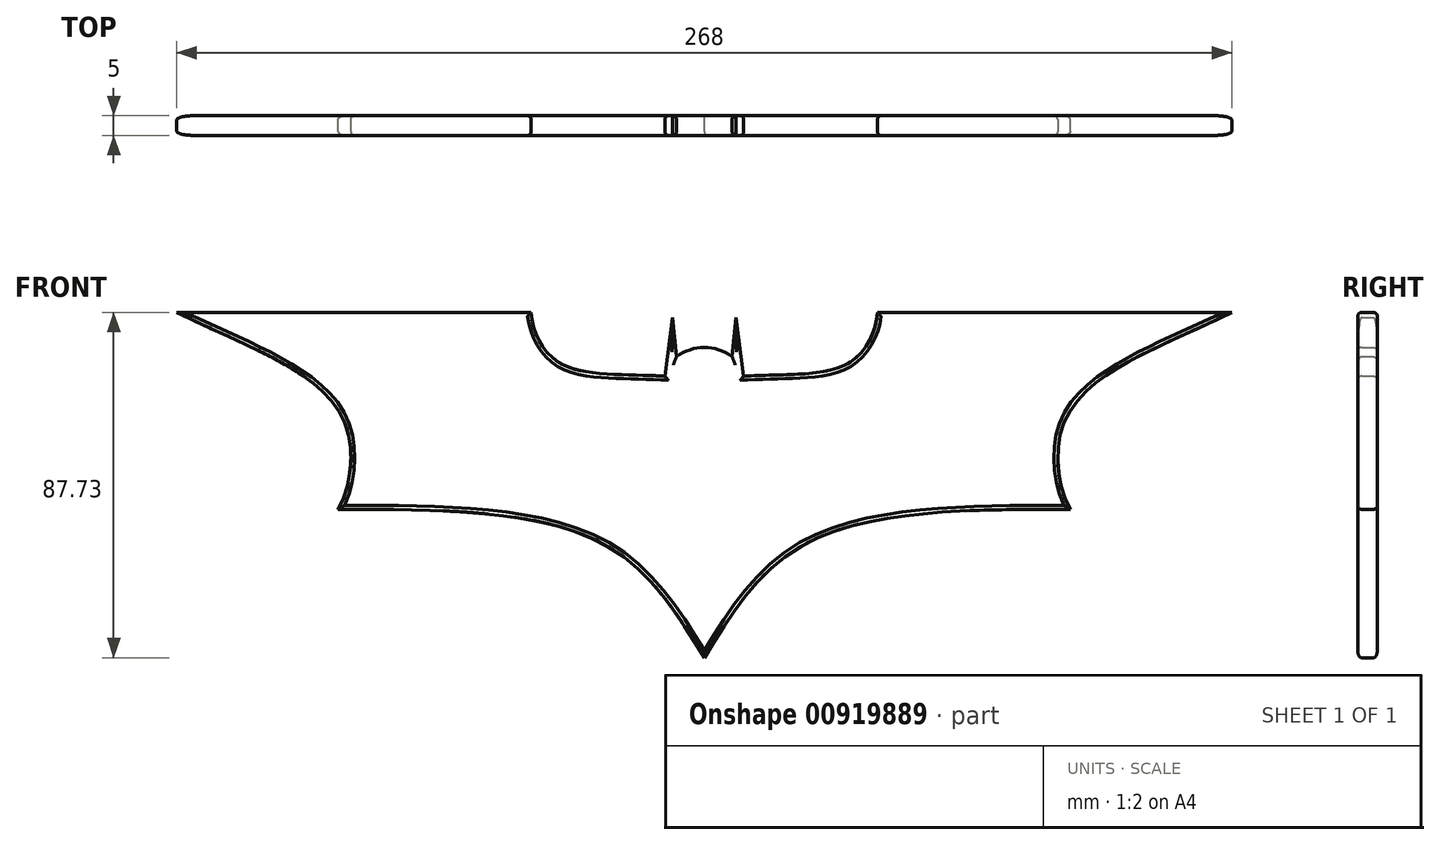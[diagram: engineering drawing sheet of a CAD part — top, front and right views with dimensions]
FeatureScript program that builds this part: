
annotation { "Feature Type Name" : "Feature", "Feature Type Description" : "" }
export const myFeature = defineFeature(function(context is Context, id is Id, definition is map)
    precondition{}
    {
        {
            var Q0;
            Q0=qCreatedBy(makeId("Front.planeOp"),FACE);
            var sketch = newSketch(context, id + "F0", { "sketchPlane" : qUnion([Q0])});
            skArc(sketch, "E0", {"start": v(7.06, 43.8) * mm, "mid": v(0, 46.17) * mm, "end": v(-7.06, 43.8) * mm});
            skLineSegment(sketch, "E1", {"start": v(-7.06, 43.8) * mm, "end": v(-8.09, 53.75) * mm});
            skLineSegment(sketch, "E2", {"start": v(-8.09, 53.75) * mm, "end": v(-10, 38.88) * mm});
            skFitSpline(sketch, "E3", {"points": [v(-10, 38.88) * mm, v(-36.7, 42.22) * mm, v(-44, 55.04) * mm], "startDerivative": vector(-67.87, 3.06) * mm, "endDerivative": vector(-3.47, 40.54) * mm});
            skLineSegment(sketch, "E4", {"start": v(-44, 55.04) * mm, "end": v(-134, 55.04) * mm});
            skFitSpline(sketch, "E5", {"points": [v(-134, 55.04) * mm, v(-92.16, 28.77) * mm, v(-93, 5.04) * mm], "startDerivative": vector(83.7, -40.96) * mm, "endDerivative": vector(-21.5, -36.05) * mm});
            skFitSpline(sketch, "E6", {"points": [v(-93, 5.04) * mm, v(-26.28, -3.43) * mm, v(0, -32.69) * mm], "startDerivative": vector(133.91, -0.06) * mm, "endDerivative": vector(48.28, -78.9) * mm});
            skFitSpline(sketch, "E7.MirrorCS", {"points": [v(93, 5.04) * mm, v(26.28, -3.43) * mm, v(0, -32.69) * mm], "startDerivative": vector(-133.91, -0.06) * mm, "endDerivative": vector(-48.28, -78.9) * mm});
            skFitSpline(sketch, "E8.MirrorCS", {"points": [v(134, 55.04) * mm, v(92.16, 28.77) * mm, v(93, 5.04) * mm], "startDerivative": vector(-83.7, -40.96) * mm, "endDerivative": vector(21.5, -36.05) * mm});
            skLineSegment(sketch, "E9.MirrorCS", {"start": v(44, 55.04) * mm, "end": v(134, 55.04) * mm});
            skFitSpline(sketch, "E10.MirrorCS", {"points": [v(10, 38.88) * mm, v(36.7, 42.22) * mm, v(44, 55.04) * mm], "startDerivative": vector(67.87, 3.06) * mm, "endDerivative": vector(3.47, 40.54) * mm});
            skLineSegment(sketch, "E11.MirrorCS", {"start": v(7.06, 43.8) * mm, "end": v(8.09, 53.75) * mm});
            skLineSegment(sketch, "E12.MirrorCS", {"start": v(8.09, 53.75) * mm, "end": v(10, 38.88) * mm});
            skSolve(sketch);
        }
        {
            var Q0;
            Q0=makeQuery(id+"F0.imprint","IMPRINT",FACE,{"disambiguationData":[TD([[makeQuery(id+"F0.imprint","IMPRINT",EDGE,{"derivedFrom":sQuery(id+"F0.wireOp",EDGE,"E0")}),1.0]])]});
            extrude(context, id + "F1", {"entities" : qUnion([Q0]), "depth" : 5 * mm});
        }
        {
            var Q0;
            Q0=makeQuery(id+"F1.opExtrude","CAP_EDGE",EDGE,{"disambiguationData":[OSD([sQuery(id+"F0.wireOp",EDGE,"E4")])],"isStart":false});
            var Q1;
            Q1=makeQuery(id+"F1.opExtrude","CAP_EDGE",EDGE,{"disambiguationData":[OSD([sQuery(id+"F0.wireOp",EDGE,"E5")])],"isStart":false});
            var Q2;
            Q2=makeQuery(id+"F1.opExtrude","CAP_EDGE",EDGE,{"disambiguationData":[OSD([sQuery(id+"F0.wireOp",EDGE,"E6")])],"isStart":false});
            var Q3;
            Q3=makeQuery(id+"F1.opExtrude","CAP_EDGE",EDGE,{"disambiguationData":[OSD([sQuery(id+"F0.wireOp",EDGE,"E7.MirrorCS")])],"isStart":false});
            var Q4;
            Q4=makeQuery(id+"F1.opExtrude","CAP_EDGE",EDGE,{"disambiguationData":[OSD([sQuery(id+"F0.wireOp",EDGE,"E8.MirrorCS")])],"isStart":false});
            var Q5;
            Q5=makeQuery(id+"F1.opExtrude","CAP_EDGE",EDGE,{"disambiguationData":[OSD([sQuery(id+"F0.wireOp",EDGE,"E9.MirrorCS")])],"isStart":false});
            var Q6;
            Q6=makeQuery(id+"F1.opExtrude","CAP_EDGE",EDGE,{"disambiguationData":[OSD([sQuery(id+"F0.wireOp",EDGE,"E11.MirrorCS")])],"isStart":false});
            var Q7;
            Q7=makeQuery(id+"F1.opExtrude","CAP_EDGE",EDGE,{"disambiguationData":[OSD([sQuery(id+"F0.wireOp",EDGE,"E1")])],"isStart":false});
            var Q8;
            Q8=makeQuery(id+"F1.opExtrude","CAP_EDGE",EDGE,{"disambiguationData":[OSD([sQuery(id+"F0.wireOp",EDGE,"E0")])],"isStart":false});
            var Q9;
            Q9=makeQuery(id+"F1.opExtrude","CAP_EDGE",EDGE,{"disambiguationData":[OSD([sQuery(id+"F0.wireOp",EDGE,"E2")])],"isStart":false});
            var Q10;
            Q10=makeQuery(id+"F1.opExtrude","CAP_EDGE",EDGE,{"disambiguationData":[OSD([sQuery(id+"F0.wireOp",EDGE,"E12.MirrorCS")])],"isStart":false});
            var Q11;
            Q11=makeQuery(id+"F1.opExtrude","CAP_EDGE",EDGE,{"disambiguationData":[OSD([sQuery(id+"F0.wireOp",EDGE,"E10.MirrorCS")])],"isStart":false});
            var Q12;
            Q12=makeQuery(id+"F1.opExtrude","CAP_EDGE",EDGE,{"disambiguationData":[OSD([sQuery(id+"F0.wireOp",EDGE,"E3")])],"isStart":false});
            var Q13;
            Q13=makeQuery(id+"F1.opExtrude","CAP_EDGE",EDGE,{"disambiguationData":[OSD([sQuery(id+"F0.wireOp",EDGE,"E12.MirrorCS")])],"isStart":true});
            var Q14;
            Q14=makeQuery(id+"F1.opExtrude","CAP_EDGE",EDGE,{"disambiguationData":[OSD([sQuery(id+"F0.wireOp",EDGE,"E11.MirrorCS")])],"isStart":true});
            var Q15;
            Q15=makeQuery(id+"F1.opExtrude","CAP_EDGE",EDGE,{"disambiguationData":[OSD([sQuery(id+"F0.wireOp",EDGE,"E0")])],"isStart":true});
            var Q16;
            Q16=makeQuery(id+"F1.opExtrude","CAP_EDGE",EDGE,{"disambiguationData":[OSD([sQuery(id+"F0.wireOp",EDGE,"E1")])],"isStart":true});
            var Q17;
            Q17=makeQuery(id+"F1.opExtrude","CAP_EDGE",EDGE,{"disambiguationData":[OSD([sQuery(id+"F0.wireOp",EDGE,"E2")])],"isStart":true});
            var Q18;
            Q18=makeQuery(id+"F1.opExtrude","CAP_EDGE",EDGE,{"disambiguationData":[OSD([sQuery(id+"F0.wireOp",EDGE,"E3")])],"isStart":true});
            var Q19;
            Q19=makeQuery(id+"F1.opExtrude","CAP_EDGE",EDGE,{"disambiguationData":[OSD([sQuery(id+"F0.wireOp",EDGE,"E10.MirrorCS")])],"isStart":true});
            var Q20;
            Q20=makeQuery(id+"F1.opExtrude","CAP_EDGE",EDGE,{"disambiguationData":[OSD([sQuery(id+"F0.wireOp",EDGE,"E9.MirrorCS")])],"isStart":true});
            var Q21;
            Q21=makeQuery(id+"F1.opExtrude","CAP_EDGE",EDGE,{"disambiguationData":[OSD([sQuery(id+"F0.wireOp",EDGE,"E8.MirrorCS")])],"isStart":true});
            var Q22;
            Q22=makeQuery(id+"F1.opExtrude","CAP_EDGE",EDGE,{"disambiguationData":[OSD([sQuery(id+"F0.wireOp",EDGE,"E7.MirrorCS")])],"isStart":true});
            var Q23;
            Q23=makeQuery(id+"F1.opExtrude","CAP_EDGE",EDGE,{"disambiguationData":[OSD([sQuery(id+"F0.wireOp",EDGE,"E6")])],"isStart":true});
            var Q24;
            Q24=makeQuery(id+"F1.opExtrude","CAP_EDGE",EDGE,{"disambiguationData":[OSD([sQuery(id+"F0.wireOp",EDGE,"E5")])],"isStart":true});
            var Q25;
            Q25=makeQuery(id+"F1.opExtrude","CAP_EDGE",EDGE,{"disambiguationData":[OSD([sQuery(id+"F0.wireOp",EDGE,"E4")])],"isStart":true});
            fillet(context, id + "F2", {"entities" : qUnion([Q0, Q1, Q2, Q3, Q4, Q5, Q6, Q7, Q8, Q9, Q10, Q11, Q12, Q13, Q14, Q15, Q16, Q17, Q18, Q19, Q20, Q21, Q22, Q23, Q24, Q25]), "radius" : 1 * mm, "tangentPropagation" : true, "allowEdgeOverflow" : false});
        }
    });
